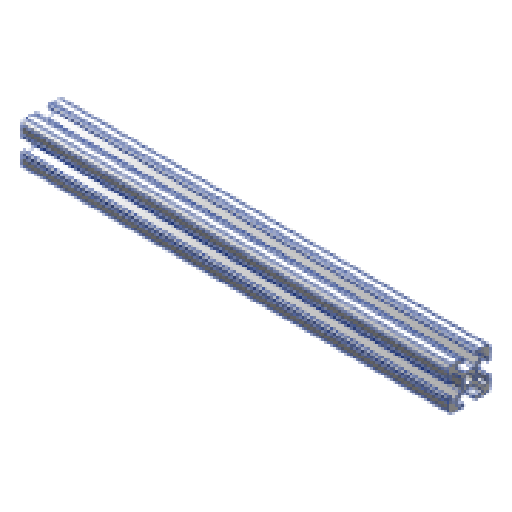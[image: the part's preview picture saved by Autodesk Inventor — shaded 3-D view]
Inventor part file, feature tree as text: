
AUTODESK INVENTOR PART (.ipt)
format: ipt  version: 2025 (Build 290162000, 162)  size: 251,904 bytes
history: native  units: in
note: dims shown in document units (in); Inventor stores cm internally (conversion verified against a paired STEP export)
features: extrude x1, sketch x1
ambient origin geometry x8: Origin, YZ Plane, XZ Plane, XY Plane, X Axis, Y Axis, Z Axis, Center Point
bodies: Solid1 (feature_tree)
feature tree (2):
  extrude  "Extrusion1"  [1 undecoded]
  sketch  "Sketch1"  dims[d0=10.0in d1=0.0in]
note: 1 required parameter value undecoded (feature->parameter linkage not recoverable at this tier; creation-order binding heuristic only, values carry confidence <= 0.55)
